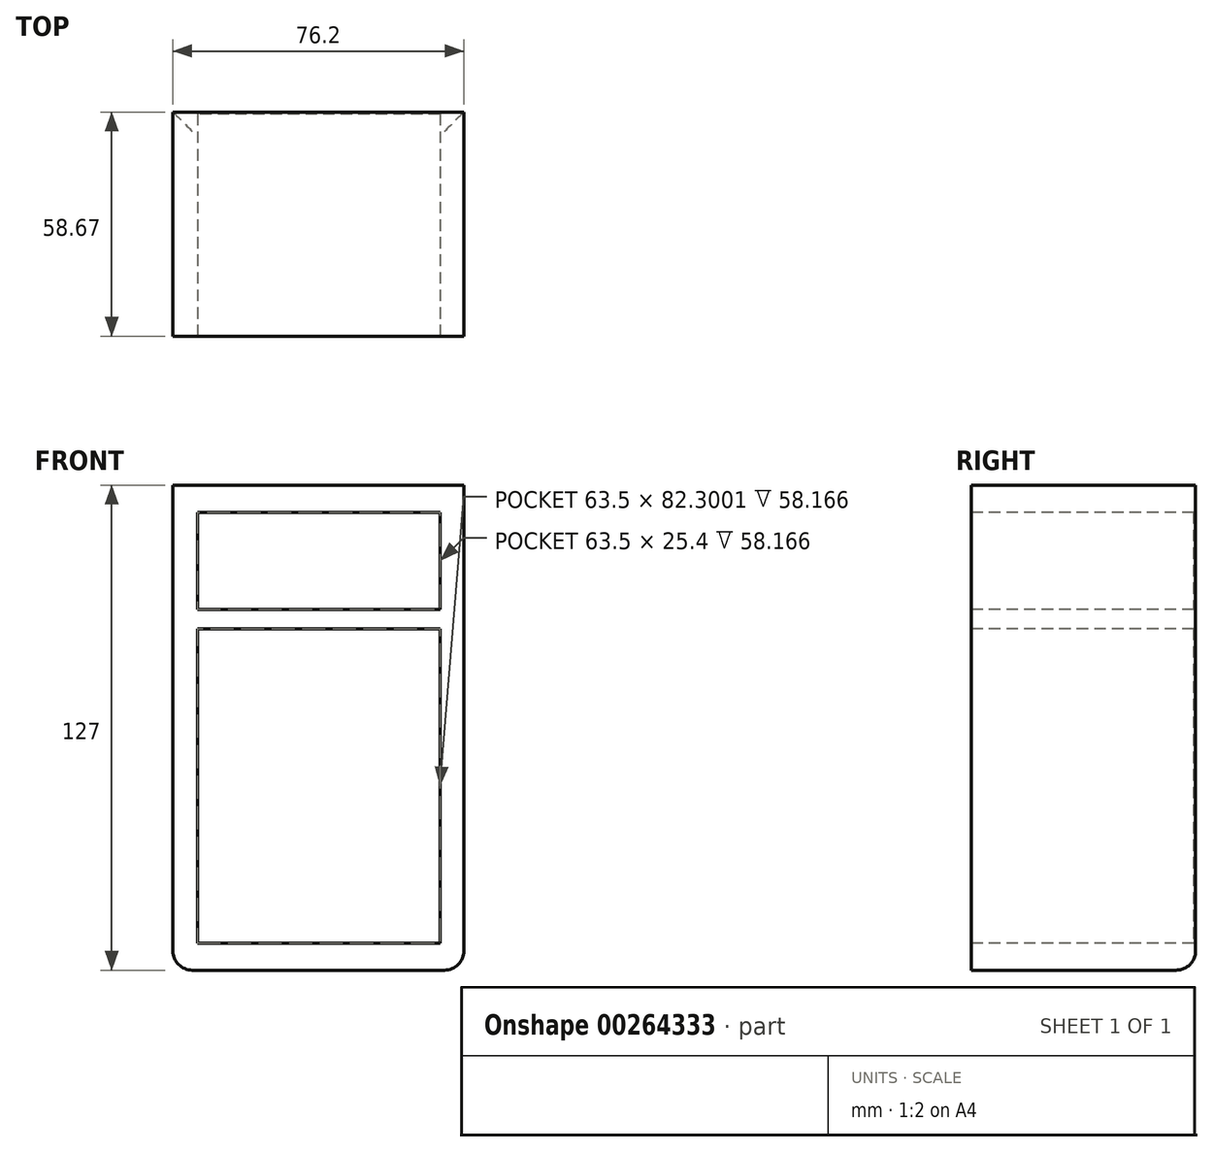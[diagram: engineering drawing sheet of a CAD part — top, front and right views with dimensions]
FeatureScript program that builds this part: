
annotation { "Feature Type Name" : "Feature", "Feature Type Description" : "" }
export const myFeature = defineFeature(function(context is Context, id is Id, definition is map)
    precondition{}
    {
        {
            var Q0;
            Q0=qCreatedBy(makeId("Front.planeOp"),FACE);
            var sketch = newSketch(context, id + "F0", { "sketchPlane" : qUnion([Q0])});
            skLineSegment(sketch, "E0.bottom", {"start": v(38.1, 63.5) * mm, "end": v(-38.1, 63.5) * mm});
            skLineSegment(sketch, "E0.top", {"start": v(38.1, -63.5) * mm, "end": v(-38.1, -63.5) * mm});
            skLineSegment(sketch, "E0.left", {"start": v(38.1, 63.5) * mm, "end": v(38.1, -63.5) * mm});
            skLineSegment(sketch, "E0.right", {"start": v(-38.1, 63.5) * mm, "end": v(-38.1, -63.5) * mm});
            skPoint(sketch, "E0.middle", {"position": v(0, 0) * mm});
            skSolve(sketch);
        }
        {
            var Q0;
            Q0 = qSketchRegion(id + "F0", true);
            extrude(context, id + "F1", {"entities" : qUnion([Q0]), "depth" : 58.67 * mm});
        }
        {
            var Q0;
            Q0=makeQuery(id+"F1.opExtrude","CAP_FACE",FACE,{"disambiguationData":[OSD([sQuery(id+"F0.wireOp",EDGE,"E0.bottom"),sQuery(id+"F0.wireOp",EDGE,"E0.top"),sQuery(id+"F0.wireOp",EDGE,"E0.left"),sQuery(id+"F0.wireOp",EDGE,"E0.right")])],"isStart":false});
            var sketch = newSketch(context, id + "F2", { "sketchPlane" : qUnion([Q0])});
            skLineSegment(sketch, "E1.bottom", {"start": v(-31.66, 56.4) * mm, "end": v(31.84, 56.4) * mm});
            skLineSegment(sketch, "E1.top", {"start": v(-31.66, 31) * mm, "end": v(31.84, 31) * mm});
            skLineSegment(sketch, "E1.left", {"start": v(-31.66, 56.4) * mm, "end": v(-31.66, 31) * mm});
            skLineSegment(sketch, "E1.right", {"start": v(31.84, 56.4) * mm, "end": v(31.84, 31) * mm});
            skLineSegment(sketch, "E2", {"start": v(31.84, 31) * mm, "end": v(31.84, -56.39) * mm});
            skLineSegment(sketch, "E3.bottom", {"start": v(31.84, -56.39) * mm, "end": v(-31.66, -56.39) * mm});
            skLineSegment(sketch, "E3.top", {"start": v(31.84, 25.91) * mm, "end": v(-31.66, 25.91) * mm});
            skLineSegment(sketch, "E3.left", {"start": v(31.84, -56.39) * mm, "end": v(31.84, 25.91) * mm});
            skLineSegment(sketch, "E3.right", {"start": v(-31.66, -56.39) * mm, "end": v(-31.66, 25.91) * mm});
            skSolve(sketch);
        }
        {
            var Q0;
            Q0=makeQuery(id+"F2.imprint","IMPRINT",FACE,{"disambiguationData":[TD([[makeQuery(id+"F2.imprint","IMPRINT",EDGE,{"derivedFrom":sQuery(id+"F2.wireOp",EDGE,"E1.bottom")}),-1.0]])]});
            var Q1;
            Q1=makeQuery(id+"F2.imprint","IMPRINT",FACE,{"disambiguationData":[TD([[makeQuery(id+"F2.imprint","IMPRINT",EDGE,{"derivedFrom":sQuery(id+"F2.wireOp",EDGE,"E3.bottom")}),-1.0]])]});
            extrude(context, id + "F3", {"entities" : qUnion([Q0, Q1]), "operationType" : NewBodyOperationType.REMOVE, "oppositeDirection" : true, "depth" : 58.17 * mm});
        }
        {
            var Q0;
            Q0=makeQuery(id+"F1.opExtrude","SWEPT_EDGE",EDGE,{"disambiguationData":[OSD([sQuery(id+"F0.wireOp",EDGE,"E0.top"),sQuery(id+"F0.wireOp",EDGE,"E0.left")])]});
            var Q1;
            Q1=makeQuery(id+"F1.opExtrude","SWEPT_EDGE",EDGE,{"disambiguationData":[OSD([sQuery(id+"F0.wireOp",EDGE,"E0.top"),sQuery(id+"F0.wireOp",EDGE,"E0.right")])]});
            var Q2;
            Q2=makeQuery(id+"F1.opExtrude","CAP_EDGE",EDGE,{"disambiguationData":[OSD([sQuery(id+"F0.wireOp",EDGE,"E0.top")])],"isStart":true});
            fillet(context, id + "F4", {"entities" : qUnion([Q0, Q1, Q2]), "radius" : 5.08 * mm, "tangentPropagation" : true, "allowEdgeOverflow" : false});
        }
    });
